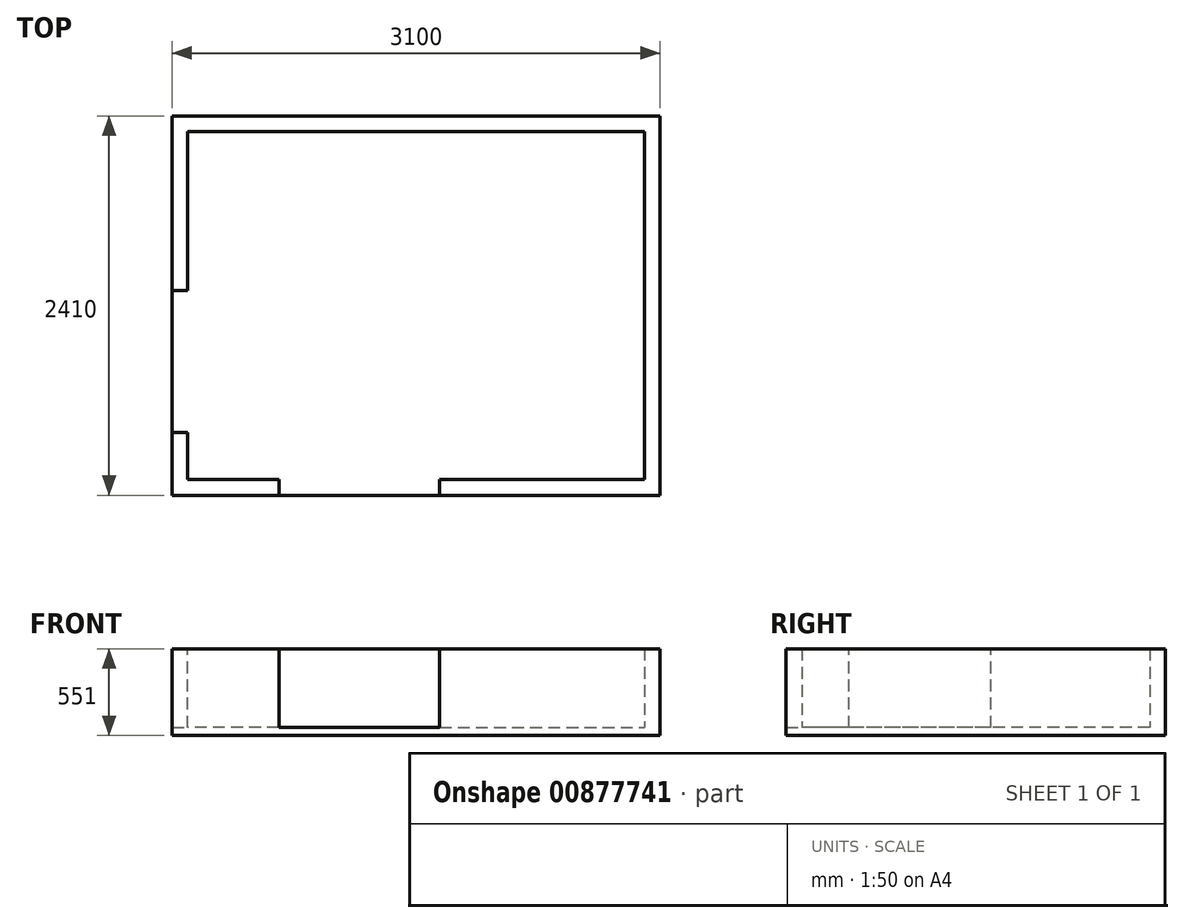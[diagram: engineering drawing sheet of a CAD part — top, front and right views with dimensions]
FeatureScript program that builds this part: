
annotation { "Feature Type Name" : "Feature", "Feature Type Description" : "" }
export const myFeature = defineFeature(function(context is Context, id is Id, definition is map)
    precondition{}
    {
        {
            var Q0;
            Q0=qCreatedBy(makeId("Top.planeOp"),FACE);
            var sketch = newSketch(context, id + "F0", { "sketchPlane" : qUnion([Q0])});
            skLineSegment(sketch, "E0.bottom", {"start": v(-1550, 1205) * mm, "end": v(1550, 1205) * mm});
            skLineSegment(sketch, "E0.top", {"start": v(-1550, -1205) * mm, "end": v(1550, -1205) * mm});
            skLineSegment(sketch, "E0.left", {"start": v(-1550, 1205) * mm, "end": v(-1550, -1205) * mm});
            skLineSegment(sketch, "E0.right", {"start": v(1550, 1205) * mm, "end": v(1550, -1205) * mm});
            skPoint(sketch, "E0.middle", {"position": v(0, 0) * mm});
            skLineSegment(sketch, "E1.bottom", {"start": v(-1450, 1105) * mm, "end": v(1450, 1105) * mm});
            skLineSegment(sketch, "E1.left", {"start": v(-1450, 1105) * mm, "end": v(-1450, -1105) * mm});
            skLineSegment(sketch, "E1.right", {"start": v(1450, 1105) * mm, "end": v(1450, -1105) * mm});
            skLineSegment(sketch, "E2", {"start": v(-870, -1205) * mm, "end": v(-870, -1105) * mm});
            skLineSegment(sketch, "E3", {"start": v(150, -1105) * mm, "end": v(150, -1205) * mm});
            skLineSegment(sketch, "E4", {"start": v(-870, -1105) * mm, "end": v(-1450, -1105) * mm});
            skLineSegment(sketch, "E5", {"start": v(150, -1105) * mm, "end": v(1450, -1105) * mm});
            skSolve(sketch);
        }
        {
            var Q0;
            Q0=makeQuery(id+"F0.imprint","IMPRINT",FACE,{"disambiguationData":[TD([[makeQuery(id+"F0.imprint","IMPRINT",EDGE,{"derivedFrom":sQuery(id+"F0.wireOp",EDGE,"E0.bottom")}),-1.0]])]});
            extrude(context, id + "F1", {"entities" : qUnion([Q0]), "depth" : 500 * mm, "offsetDistance" : 25 * mm});
        }
        {
            var Q0;
            Q0=qSketchRegion(id+"F0",true);
            extrude(context, id + "F2", {"entities" : qUnion([Q0]), "operationType" : NewBodyOperationType.ADD, "oppositeDirection" : true, "depth" : 51 * mm, "offsetDistance" : 25 * mm});
        }
        {
            var Q0;
            Q0=makeQuery(id+"F1.opExtrude","SWEPT_FACE",FACE,{"disambiguationData":[OSD([sQuery(id+"F0.wireOp",EDGE,"E1.left")])]});
            var sketch = newSketch(context, id + "F3", { "sketchPlane" : qUnion([Q0])});
            skLineSegment(sketch, "E6.bottom", {"start": v(-805, 0) * mm, "end": v(95, 0) * mm});
            skLineSegment(sketch, "E6.top", {"start": v(-805, 500) * mm, "end": v(95, 500) * mm});
            skLineSegment(sketch, "E6.left", {"start": v(-805, 0) * mm, "end": v(-805, 500) * mm});
            skLineSegment(sketch, "E6.right", {"start": v(95, 0) * mm, "end": v(95, 500) * mm});
            skSolve(sketch);
        }
        {
            var Q0;
            Q0=qSketchRegion(id+"F3",true);
            extrude(context, id + "F4", {"entities" : qUnion([Q0]), "operationType" : NewBodyOperationType.REMOVE, "oppositeDirection" : true, "depth" : 190 * mm, "offsetDistance" : 25 * mm});
        }
    });
